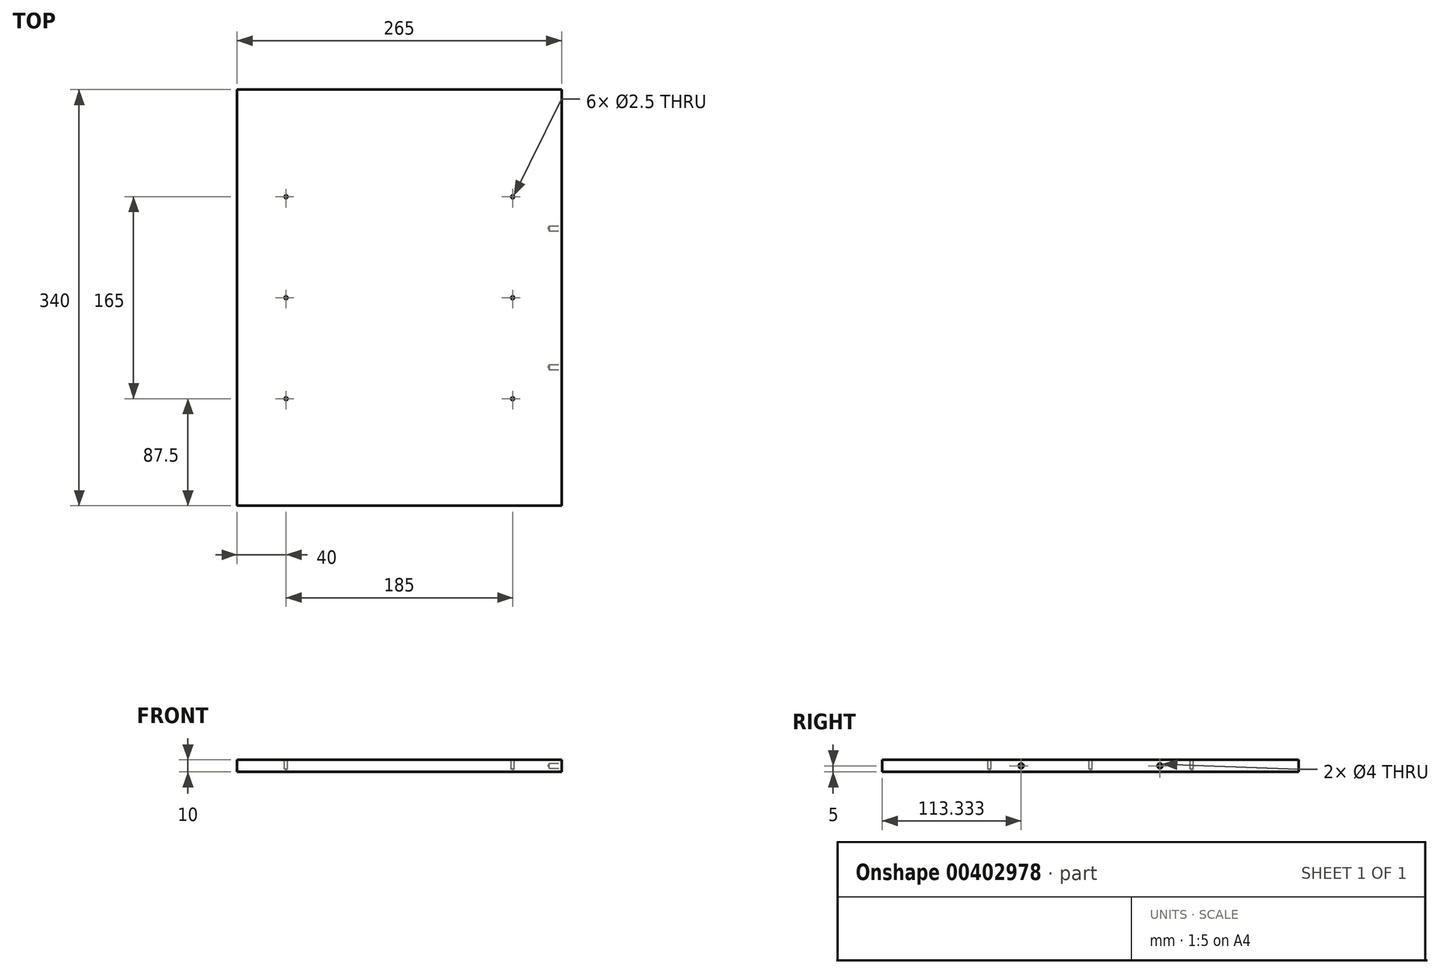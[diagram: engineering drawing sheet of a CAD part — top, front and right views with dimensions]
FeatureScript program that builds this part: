
annotation { "Feature Type Name" : "Feature", "Feature Type Description" : "" }
export const myFeature = defineFeature(function(context is Context, id is Id, definition is map)
    precondition{}
    {
        {
            var Q0;
            Q0=qCreatedBy(makeId("Top.planeOp"),FACE);
            var sketch = newSketch(context, id + "F0", { "sketchPlane" : qUnion([Q0])});
            skLineSegment(sketch, "E0.bottom", {"start": v(-132.5, 170) * mm, "end": v(132.5, 170) * mm});
            skLineSegment(sketch, "E0.top", {"start": v(-132.5, -170) * mm, "end": v(132.5, -170) * mm});
            skLineSegment(sketch, "E0.left", {"start": v(-132.5, 170) * mm, "end": v(-132.5, -170) * mm});
            skLineSegment(sketch, "E0.right", {"start": v(132.5, 170) * mm, "end": v(132.5, -170) * mm});
            skPoint(sketch, "E0.middle", {"position": v(0, 0) * mm});
            skSolve(sketch);
        }
        {
            var Q0;
            Q0=makeQuery(id+"F0.imprint","IMPRINT",FACE,{"disambiguationData":[TD([[makeQuery(id+"F0.imprint","IMPRINT",EDGE,{"derivedFrom":sQuery(id+"F0.wireOp",EDGE,"E0.bottom")}),-1.0]])]});
            extrude(context, id + "F1", {"entities" : qUnion([Q0]), "oppositeDirection" : true, "depth" : 10 * mm});
        }
        {
            var Q0;
            Q0=makeQuery(id+"F1.opExtrude","CAP_FACE",FACE,{"disambiguationData":[OSD([sQuery(id+"F0.wireOp",EDGE,"E0.bottom"),sQuery(id+"F0.wireOp",EDGE,"E0.top"),sQuery(id+"F0.wireOp",EDGE,"E0.left"),sQuery(id+"F0.wireOp",EDGE,"E0.right")])],"isStart":true});
            var sketch = newSketch(context, id + "F2", { "sketchPlane" : qUnion([Q0])});
            skPoint(sketch, "E1", {"position": v(92.5, 82.5) * mm});
            skPoint(sketch, "E2", {"position": v(92.5, 0) * mm});
            skPoint(sketch, "E3", {"position": v(92.5, -82.5) * mm});
            skPoint(sketch, "E4", {"position": v(-92.5, -82.5) * mm});
            skPoint(sketch, "E5", {"position": v(-92.5, 0) * mm});
            skPoint(sketch, "E6", {"position": v(-92.5, 82.5) * mm});
            skSolve(sketch);
        }
        {
            var Q0;
            Q0=sQuery(id+"F2.wireOp",VERTEX,"E6");
            var Q1;
            Q1=sQuery(id+"F2.wireOp",VERTEX,"E5");
            var Q2;
            Q2=sQuery(id+"F2.wireOp",VERTEX,"E4");
            var Q3;
            Q3=sQuery(id+"F2.wireOp",VERTEX,"E3");
            var Q4;
            Q4=sQuery(id+"F2.wireOp",VERTEX,"E2");
            var Q5;
            Q5=sQuery(id+"F2.wireOp",VERTEX,"E1");
            var Q6;
            Q6=makeQuery(id+"F1.opExtrude","SWEPT_BODY",BODY,{"disambiguationData":[OSD([sQuery(id+"F0.wireOp",EDGE,"E0.bottom"),sQuery(id+"F0.wireOp",EDGE,"E0.top"),sQuery(id+"F0.wireOp",EDGE,"E0.left"),sQuery(id+"F0.wireOp",EDGE,"E0.right")])]});
            hole(context, id + "F3", {"style" : HoleStyle.SIMPLE, "endStyle" : HoleEndStyle.BLIND, "holeDiameter" : 2.5 * mm, "holeDepth" : 7.5 * mm, "isTappedThrough" : true, "tappedDepth" : 12 * mm, "tapClearance" : 3, "startFromSketch" : true, "locations" : qUnion([Q0, Q1, Q2, Q3, Q4, Q5]), "scope" : qUnion([Q6])});
        }
        {
            var Q0;
            Q0=makeQuery(id+"F1.opExtrude","SWEPT_FACE",FACE,{"disambiguationData":[OSD([sQuery(id+"F0.wireOp",EDGE,"E0.right")])]});
            var sketch = newSketch(context, id + "F4", { "sketchPlane" : qUnion([Q0])});
            skPoint(sketch, "E7", {"position": v(-56.67, -5) * mm});
            skPoint(sketch, "E8", {"position": v(56.67, -5) * mm});
            skSolve(sketch);
        }
        {
            var Q0;
            Q0=sQuery(id+"F4.wireOp",VERTEX,"E7");
            var Q1;
            Q1=sQuery(id+"F4.wireOp",VERTEX,"E8");
            var Q2;
            Q2=makeQuery(id+"F1.opExtrude","SWEPT_BODY",BODY,{"disambiguationData":[OSD([sQuery(id+"F0.wireOp",EDGE,"E0.bottom"),sQuery(id+"F0.wireOp",EDGE,"E0.top"),sQuery(id+"F0.wireOp",EDGE,"E0.left"),sQuery(id+"F0.wireOp",EDGE,"E0.right")])]});
            hole(context, id + "F5", {"style" : HoleStyle.SIMPLE, "endStyle" : HoleEndStyle.BLIND, "holeDiameter" : 4 * mm, "holeDepth" : 10 * mm, "isTappedThrough" : true, "tappedDepth" : 12 * mm, "tapClearance" : 3, "startFromSketch" : true, "locations" : qUnion([Q0, Q1]), "scope" : qUnion([Q2])});
        }
    });
